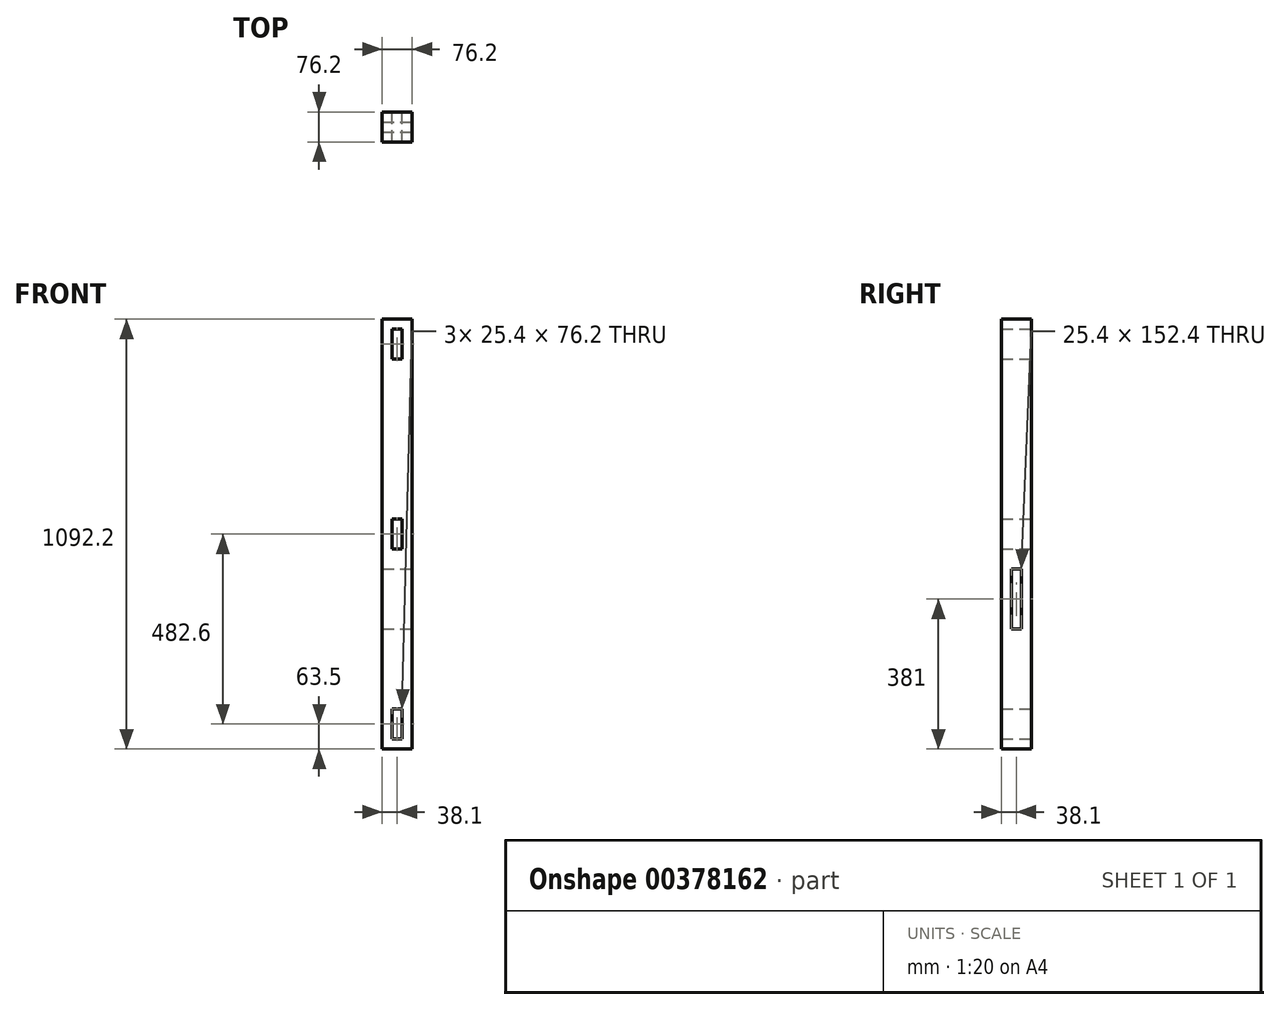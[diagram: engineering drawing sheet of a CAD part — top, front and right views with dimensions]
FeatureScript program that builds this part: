
annotation { "Feature Type Name" : "Feature", "Feature Type Description" : "" }
export const myFeature = defineFeature(function(context is Context, id is Id, definition is map)
    precondition{}
    {
        {
            var Q0;
            Q0=qCreatedBy(makeId("Front.planeOp"),FACE);
            var sketch = newSketch(context, id + "F0", { "sketchPlane" : qUnion([Q0])});
            skLineSegment(sketch, "E0.bottom", {"start": v(-38.1, 546.1) * mm, "end": v(38.1, 546.1) * mm});
            skLineSegment(sketch, "E0.top", {"start": v(-38.1, -546.1) * mm, "end": v(38.1, -546.1) * mm});
            skLineSegment(sketch, "E0.left", {"start": v(-38.1, 546.1) * mm, "end": v(-38.1, -546.1) * mm});
            skLineSegment(sketch, "E0.right", {"start": v(38.1, 546.1) * mm, "end": v(38.1, -546.1) * mm});
            skLineSegment(sketch, "E1.bottom", {"start": v(-12.7, 520.7) * mm, "end": v(12.7, 520.7) * mm});
            skLineSegment(sketch, "E1.top", {"start": v(-12.7, 444.5) * mm, "end": v(12.7, 444.5) * mm});
            skLineSegment(sketch, "E1.left", {"start": v(-12.7, 520.7) * mm, "end": v(-12.7, 444.5) * mm});
            skLineSegment(sketch, "E1.right", {"start": v(12.7, 520.7) * mm, "end": v(12.7, 444.5) * mm});
            skLineSegment(sketch, "E2.bottom", {"start": v(-12.7, 38.1) * mm, "end": v(12.7, 38.1) * mm});
            skLineSegment(sketch, "E2.top", {"start": v(-12.7, -38.1) * mm, "end": v(12.7, -38.1) * mm});
            skLineSegment(sketch, "E2.left", {"start": v(-12.7, 38.1) * mm, "end": v(-12.7, -38.1) * mm});
            skLineSegment(sketch, "E2.right", {"start": v(12.7, 38.1) * mm, "end": v(12.7, -38.1) * mm});
            skLineSegment(sketch, "E3.bottom", {"start": v(-12.7, -444.5) * mm, "end": v(12.7, -444.5) * mm});
            skLineSegment(sketch, "E3.top", {"start": v(-12.7, -520.7) * mm, "end": v(12.7, -520.7) * mm});
            skLineSegment(sketch, "E3.left", {"start": v(-12.7, -444.5) * mm, "end": v(-12.7, -520.7) * mm});
            skLineSegment(sketch, "E3.right", {"start": v(12.7, -444.5) * mm, "end": v(12.7, -520.7) * mm});
            skSolve(sketch);
        }
        {
            var Q0;
            Q0 = qSketchRegion(id + "F0", true);
            extrude(context, id + "F1", {"entities" : qUnion([Q0]), "depth" : 38.1 * mm, "hasSecondDirection" : true, "secondDirectionOppositeDirection" : true, "secondDirectionDepth" : 38.1 * mm});
        }
        {
            var Q0;
            Q0=makeQuery(id+"F1.opExtrude","SWEPT_FACE",FACE,{"disambiguationData":[OSD([sQuery(id+"F0.wireOp",EDGE,"E0.right")])]});
            var sketch = newSketch(context, id + "F2", { "sketchPlane" : qUnion([Q0])});
            skLineSegment(sketch, "E4.bottom", {"start": v(-12.7, -88.9) * mm, "end": v(12.7, -88.9) * mm});
            skLineSegment(sketch, "E4.top", {"start": v(-12.7, -241.3) * mm, "end": v(12.7, -241.3) * mm});
            skLineSegment(sketch, "E4.left", {"start": v(-12.7, -88.9) * mm, "end": v(-12.7, -241.3) * mm});
            skLineSegment(sketch, "E4.right", {"start": v(12.7, -88.9) * mm, "end": v(12.7, -241.3) * mm});
            skSolve(sketch);
        }
        {
            var Q0;
            Q0 = qSketchRegion(id + "F2", true);
            extrude(context, id + "F3", {"entities" : qUnion([Q0]), "operationType" : NewBodyOperationType.REMOVE, "oppositeDirection" : true, "depth" : 101.6 * mm});
        }
    });
